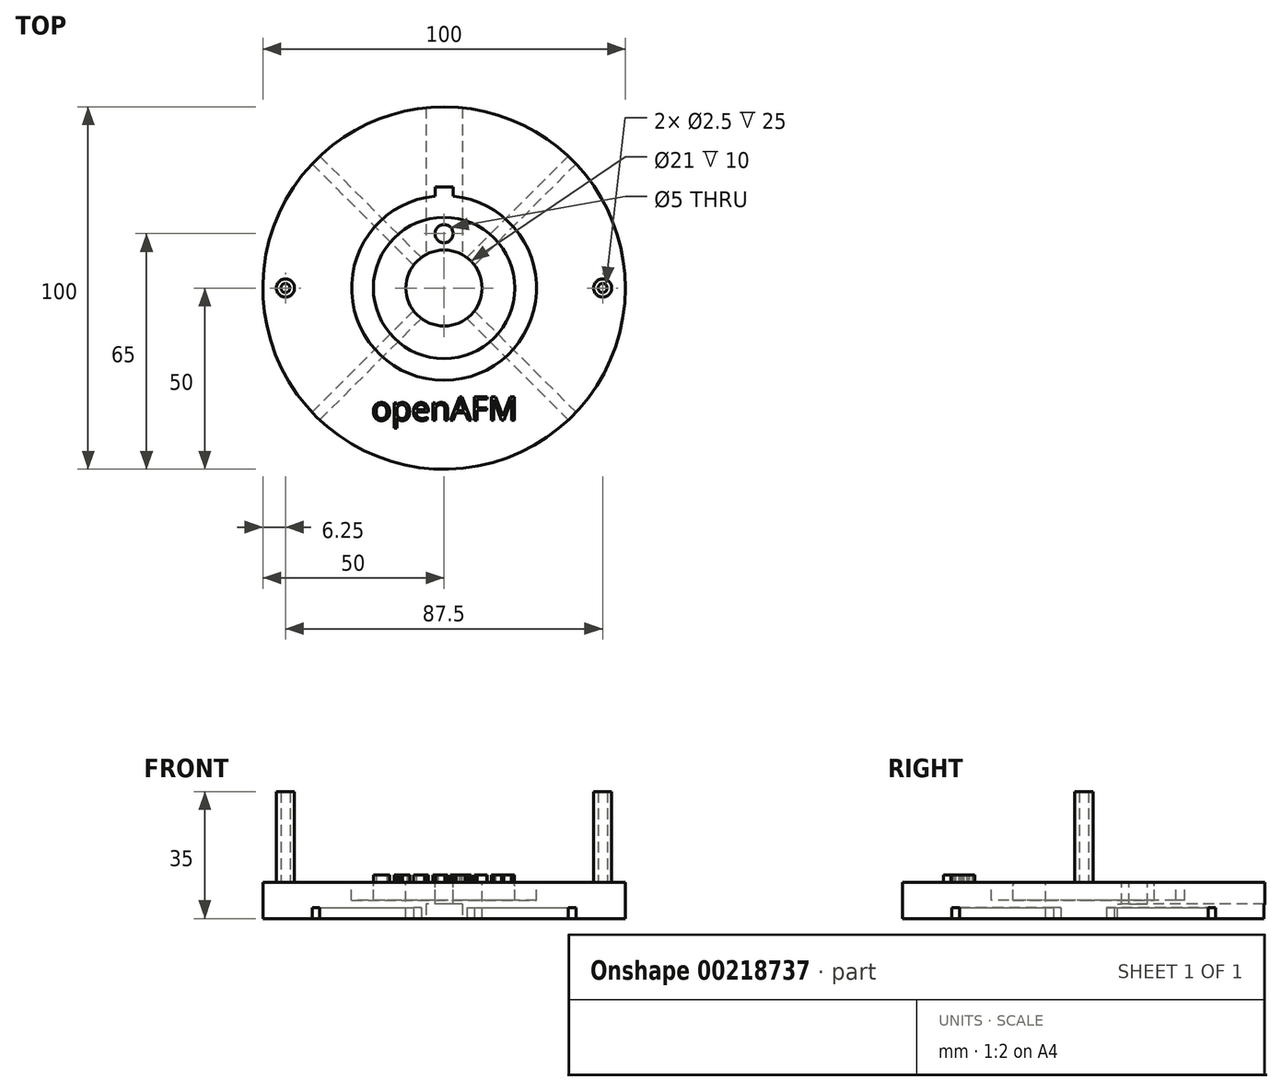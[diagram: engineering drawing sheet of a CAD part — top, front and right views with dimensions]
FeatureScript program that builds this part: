
annotation { "Feature Type Name" : "Feature", "Feature Type Description" : "" }
export const myFeature = defineFeature(function(context is Context, id is Id, definition is map)
    precondition{}
    {
        {
            var Q0;
            Q0=qCreatedBy(makeId("Top.planeOp"),FACE);
            var sketch = newSketch(context, id + "F0", { "sketchPlane" : qUnion([Q0])});
            skCircle(sketch, "E0", {"center": v(0, 0) * mm, "radius": 50 * mm});
            skSolve(sketch);
        }
        {
            var Q0;
            Q0=makeQuery(id+"F0.imprint","IMPRINT",FACE,{"disambiguationData":[TD([[makeQuery(id+"F0.imprint","IMPRINT",EDGE,{"derivedFrom":sQuery(id+"F0.wireOp",EDGE,"E0")}),1.0]])]});
            extrude(context, id + "F1", {"entities" : qUnion([Q0]), "depth" : 10 * mm});
        }
        {
            var Q0;
            Q0=makeQuery(id+"F1.opExtrude","CAP_FACE",FACE,{"disambiguationData":[OSD([sQuery(id+"F0.wireOp",EDGE,"E0")])],"isStart":false});
            var sketch = newSketch(context, id + "F2", { "sketchPlane" : qUnion([Q0])});
            skCircle(sketch, "E1", {"center": v(0, 0) * mm, "radius": 10.5 * mm});
            skSolve(sketch);
        }
        {
            var Q0;
            Q0=makeQuery(id+"F2.imprint","IMPRINT",FACE,{"disambiguationData":[TD([[makeQuery(id+"F2.imprint","IMPRINT",EDGE,{"derivedFrom":sQuery(id+"F2.wireOp",EDGE,"E1")}),1.0]])]});
            extrude(context, id + "F3", {"entities" : qUnion([Q0]), "operationType" : NewBodyOperationType.REMOVE, "oppositeDirection" : true, "depth" : 10 * mm});
        }
        {
            var Q0;
            Q0=makeQuery(id+"F1.opExtrude","CAP_FACE",FACE,{"disambiguationData":[OSD([sQuery(id+"F0.wireOp",EDGE,"E0")])],"isStart":true});
            var sketch = newSketch(context, id + "F4", { "sketchPlane" : qUnion([Q0])});
            skLineSegment(sketch, "E2", {"start": v(0, 0) * mm, "end": v(50, 0) * mm, "construction": true});
            skLineSegment(sketch, "E3", {"start": v(0, 0) * mm, "end": v(0, 50) * mm, "construction": true});
            skLineSegment(sketch, "E4", {"start": v(0, 0) * mm, "end": v(-50, 0) * mm, "construction": true});
            skLineSegment(sketch, "E5", {"start": v(0, 0) * mm, "end": v(0, -50) * mm, "construction": true});
            skLineSegment(sketch, "E6", {"start": v(0, 0) * mm, "end": v(-35.36, 35.36) * mm, "construction": true});
            skLineSegment(sketch, "E7", {"start": v(0, 0) * mm, "end": v(35.36, -35.36) * mm, "construction": true});
            skLineSegment(sketch, "E8", {"start": v(0, 0) * mm, "end": v(35.36, 35.36) * mm, "construction": true});
            skLineSegment(sketch, "E9", {"start": v(0, 0) * mm, "end": v(-35.36, -35.36) * mm, "construction": true});
            skLineSegment(sketch, "E10", {"start": v(-36.4, 34.28) * mm, "end": v(-8.4, 6.29) * mm});
            skLineSegment(sketch, "E11", {"start": v(-34.28, 36.4) * mm, "end": v(-6.29, 8.4) * mm});
            skArc(sketch, "E12", {"start": v(-8.4, -6.29) * mm, "mid": v(-7.42, -7.42) * mm, "end": v(-6.29, -8.4) * mm});
            skLineSegment(sketch, "E13.trimOffspring", {"start": v(6.29, -8.4) * mm, "end": v(34.28, -36.4) * mm});
            skLineSegment(sketch, "E14.trimOffspring", {"start": v(8.4, -6.29) * mm, "end": v(36.4, -34.28) * mm});
            skArc(sketch, "E15", {"start": v(-36.4, -34.28) * mm, "mid": v(-35.36, -35.36) * mm, "end": v(-34.28, -36.4) * mm});
            skLineSegment(sketch, "E16", {"start": v(-36.4, -34.28) * mm, "end": v(-8.4, -6.29) * mm});
            skLineSegment(sketch, "E17", {"start": v(-34.28, -36.4) * mm, "end": v(-6.29, -8.4) * mm});
            skLineSegment(sketch, "E18.trimOffspring", {"start": v(6.29, 8.4) * mm, "end": v(34.28, 36.4) * mm});
            skLineSegment(sketch, "E19.trimOffspring", {"start": v(8.4, 6.29) * mm, "end": v(36.4, 34.28) * mm});
            skArc(sketch, "E20.trimOffspring", {"start": v(-34.28, 36.4) * mm, "mid": v(-35.36, 35.36) * mm, "end": v(-36.4, 34.28) * mm});
            skArc(sketch, "E21.trimOffspring", {"start": v(36.4, 34.28) * mm, "mid": v(35.36, 35.36) * mm, "end": v(34.28, 36.4) * mm});
            skArc(sketch, "E22.trimOffspring", {"start": v(34.28, -36.4) * mm, "mid": v(35.36, -35.36) * mm, "end": v(36.4, -34.28) * mm});
            skArc(sketch, "E23.trimOffspring", {"start": v(-6.29, 8.4) * mm, "mid": v(-7.42, 7.42) * mm, "end": v(-8.4, 6.29) * mm});
            skArc(sketch, "E24.trimOffspring", {"start": v(8.4, 6.29) * mm, "mid": v(7.42, 7.42) * mm, "end": v(6.29, 8.4) * mm});
            skArc(sketch, "E25.trimOffspring", {"start": v(6.29, -8.4) * mm, "mid": v(7.42, -7.42) * mm, "end": v(8.4, -6.29) * mm});
            skLineSegment(sketch, "E26", {"start": v(-2.5, 10.2) * mm, "end": v(-2.5, 49.94) * mm});
            skLineSegment(sketch, "E27", {"start": v(2.5, 10.2) * mm, "end": v(2.5, 49.94) * mm});
            skLineSegment(sketch, "E28", {"start": v(2.5, 49.94) * mm, "end": v(2.93, 49.2) * mm});
            skArc(sketch, "E29", {"start": v(-2.5, 10.2) * mm, "mid": v(0, 10.5) * mm, "end": v(2.5, 10.2) * mm});
            skArc(sketch, "E30", {"start": v(-2.5, 49.94) * mm, "mid": v(0, 50) * mm, "end": v(2.5, 49.94) * mm});
            skSolve(sketch);
        }
        {
            var Q0;
            Q0=makeQuery(id+"F4.imprint","IMPRINT",FACE,{"disambiguationData":[TD([[makeQuery(id+"F4.imprint","IMPRINT",EDGE,{"derivedFrom":sQuery(id+"F4.wireOp",EDGE,"E10")}),1.0]])]});
            var Q1;
            Q1=makeQuery(id+"F4.imprint","IMPRINT",FACE,{"disambiguationData":[TD([[makeQuery(id+"F4.imprint","IMPRINT",EDGE,{"derivedFrom":sQuery(id+"F4.wireOp",EDGE,"E18.trimOffspring")}),-1.0]])]});
            var Q2;
            Q2=makeQuery(id+"F4.imprint","IMPRINT",FACE,{"disambiguationData":[TD([[makeQuery(id+"F4.imprint","IMPRINT",EDGE,{"derivedFrom":sQuery(id+"F4.wireOp",EDGE,"E13.trimOffspring")}),1.0]])]});
            var Q3;
            Q3=makeQuery(id+"F4.imprint","IMPRINT",FACE,{"disambiguationData":[TD([[makeQuery(id+"F4.imprint","IMPRINT",EDGE,{"derivedFrom":sQuery(id+"F4.wireOp",EDGE,"E12")}),1.0]])]});
            extrude(context, id + "F5", {"entities" : qUnion([Q0, Q1, Q2, Q3]), "operationType" : NewBodyOperationType.REMOVE, "oppositeDirection" : true, "depth" : 3 * mm});
        }
        {
            var Q0;
            Q0=makeQuery(id+"F1.opExtrude","CAP_FACE",FACE,{"disambiguationData":[OSD([sQuery(id+"F0.wireOp",EDGE,"E0")])],"isStart":false});
            var sketch = newSketch(context, id + "F6", { "sketchPlane" : qUnion([Q0])});
            skCircle(sketch, "E31", {"center": v(0, 0) * mm, "radius": 19.5 * mm});
            skCircle(sketch, "E32", {"center": v(0, 0) * mm, "radius": 25.5 * mm});
            skSolve(sketch);
        }
        {
            var Q0;
            Q0=makeQuery(id+"F6.imprint","IMPRINT",FACE,{"disambiguationData":[TD([[makeQuery(id+"F6.imprint","IMPRINT",EDGE,{"derivedFrom":sQuery(id+"F6.wireOp",EDGE,"E31")}),-1.0]])]});
            extrude(context, id + "F7", {"entities" : qUnion([Q0]), "operationType" : NewBodyOperationType.REMOVE, "oppositeDirection" : true, "depth" : 5 * mm});
        }
        {
            var Q0;
            {var subQ0=sQuery(id+"F0.wireOp",EDGE,"E0");Q0=makeQuery(id+"F7.boolean.opBoolean","SPLIT",FACE,{"disambiguationData":[TD([makeQuery(id+"F1.opExtrude","SWEPT_FACE",FACE,{"disambiguationData":[OSD([subQ0])]})])],"derivedFrom":makeQuery(id+"F1.opExtrude","CAP_FACE",FACE,{"disambiguationData":[OSD([subQ0])],"isStart":false})});}
            var sketch = newSketch(context, id + "F8", { "sketchPlane" : qUnion([Q0])});
            skCircle(sketch, "E33", {"center": v(-43.75, 0) * mm, "radius": 2.5 * mm});
            skCircle(sketch, "E34", {"center": v(-43.75, 0) * mm, "radius": 1.25 * mm});
            skCircle(sketch, "E35", {"center": v(43.75, 0) * mm, "radius": 2.5 * mm});
            skCircle(sketch, "E36", {"center": v(43.75, 0) * mm, "radius": 1.25 * mm});
            skSolve(sketch);
        }
        {
            var Q0;
            Q0 = qSketchRegion(id + "F8", true);
            extrude(context, id + "F9", {"entities" : qUnion([Q0]), "operationType" : NewBodyOperationType.ADD, "depth" : 25 * mm});
        }
        {
            var Q0;
            Q0=makeQuery(id+"F7.boolean.opBoolean","COPY",EDGE,{"derivedFrom":makeQuery(id+"F7.opExtrude","CAP_EDGE",EDGE,{"disambiguationData":[OSD([sQuery(id+"F6.wireOp",EDGE,"E31")])],"isStart":true})});
            var Q1;
            Q1=makeQuery(id+"F7.boolean.opBoolean","COPY",EDGE,{"derivedFrom":makeQuery(id+"F7.opExtrude","CAP_EDGE",EDGE,{"disambiguationData":[OSD([sQuery(id+"F6.wireOp",EDGE,"E32")])],"isStart":true})});
            fillet(context, id + "F10", {"entities" : qUnion([Q0, Q1]), "radius" : 1 * mm, "tangentPropagation" : true, "allowEdgeOverflow" : false});
        }
        {
            var Q0;
            Q0=makeQuery(id+"F7.boolean.opBoolean","SPLIT",FACE,{"disambiguationData":[TD([makeQuery(id+"F3.boolean.opBoolean","COPY",FACE,{"derivedFrom":makeQuery(id+"F3.opExtrude","SWEPT_FACE",FACE,{"disambiguationData":[OSD([sQuery(id+"F2.wireOp",EDGE,"E1")])]})})])],"derivedFrom":makeQuery(id+"F1.opExtrude","CAP_FACE",FACE,{"disambiguationData":[OSD([sQuery(id+"F0.wireOp",EDGE,"E0")])],"isStart":false})});
            var sketch = newSketch(context, id + "F11", { "sketchPlane" : qUnion([Q0])});
            skCircle(sketch, "E37", {"center": v(0, 15) * mm, "radius": 2.5 * mm});
            skSolve(sketch);
        }
        {
            var Q0;
            Q0 = qSketchRegion(id + "F11", true);
            extrude(context, id + "F12", {"entities" : qUnion([Q0]), "operationType" : NewBodyOperationType.REMOVE, "oppositeDirection" : true, "depth" : 10 * mm});
        }
        {
            var Q0;
            Q0=qCreatedBy(makeId("Front.planeOp"),FACE);
            var sketch = newSketch(context, id + "F13", { "sketchPlane" : qUnion([Q0])});
            skLineSegment(sketch, "E38", {"start": v(-5, 4) * mm, "end": v(-5, 0) * mm});
            skLineSegment(sketch, "E39", {"start": v(-5, 0) * mm, "end": v(5, 0) * mm});
            skLineSegment(sketch, "E40", {"start": v(5, 0) * mm, "end": v(5, 4) * mm});
            skLineSegment(sketch, "E41", {"start": v(5, 4) * mm, "end": v(-5, 4) * mm});
            skSolve(sketch);
        }
        {
            var Q0;
            Q0 = qSketchRegion(id + "F13", true);
            extrude(context, id + "F14", {"entities" : qUnion([Q0]), "operationType" : NewBodyOperationType.REMOVE, "oppositeDirection" : true, "depth" : 50 * mm});
        }
        {
            var Q0;
            {var subQ0=sQuery(id+"F0.wireOp",EDGE,"E0");var subQ1=makeQuery(id+"F1.opExtrude","SWEPT_FACE",FACE,{"disambiguationData":[OSD([subQ0])]});Q0=makeQuery(id+"F9.boolean.opBoolean","SPLIT",FACE,{"disambiguationData":[TD([subQ1])],"derivedFrom":makeQuery(id+"F7.boolean.opBoolean","SPLIT",FACE,{"disambiguationData":[TD([subQ1])],"derivedFrom":makeQuery(id+"F1.opExtrude","CAP_FACE",FACE,{"disambiguationData":[OSD([subQ0])],"isStart":false})})});}
            var sketch = newSketch(context, id + "F15", { "sketchPlane" : qUnion([Q0])});
            skArc(sketch, "E42", {"start": v(2.5, 25.38) * mm, "mid": v(0, 25.5) * mm, "end": v(-2.5, 25.38) * mm});
            skLineSegment(sketch, "E43", {"start": v(0, 0) * mm, "end": v(0, 32.13) * mm, "construction": true});
            skLineSegment(sketch, "E44", {"start": v(-2.5, 25.38) * mm, "end": v(-2.5, 27.88) * mm});
            skLineSegment(sketch, "E45", {"start": v(-2.5, 27.88) * mm, "end": v(2.5, 27.88) * mm});
            skLineSegment(sketch, "E46", {"start": v(2.5, 27.88) * mm, "end": v(2.5, 25.38) * mm});
            skSolve(sketch);
        }
        {
            var Q0;
            Q0 = qSketchRegion(id + "F15", true);
            extrude(context, id + "F16", {"entities" : qUnion([Q0]), "operationType" : NewBodyOperationType.REMOVE, "oppositeDirection" : true, "depth" : 5 * mm});
        }
        {
            var Q0;
            {var subQ0=sQuery(id+"F0.wireOp",EDGE,"E0");var subQ1=makeQuery(id+"F1.opExtrude","SWEPT_FACE",FACE,{"disambiguationData":[OSD([subQ0])]});Q0=makeQuery(id+"F9.boolean.opBoolean","SPLIT",FACE,{"disambiguationData":[TD([subQ1])],"derivedFrom":makeQuery(id+"F7.boolean.opBoolean","SPLIT",FACE,{"disambiguationData":[TD([subQ1])],"derivedFrom":makeQuery(id+"F1.opExtrude","CAP_FACE",FACE,{"disambiguationData":[OSD([subQ0])],"isStart":false})})});}
            var sketch = newSketch(context, id + "F17", { "sketchPlane" : qUnion([Q0])});
            skText(sketch, "E47", { "text": "openAFM\n", "fontName": "OpenSans-Regular.ttf"});
            const initialGuessF17  = {"E47": [-0.02, -0.03653, 1, 0, 0.00653]};
            skSetInitialGuess(sketch, initialGuessF17);
            skSolve(sketch);
        }
        {
            var Q0;
            Q0 = qSketchRegion(id + "F17", true);
            extrude(context, id + "F18", {"entities" : qUnion([Q0]), "operationType" : NewBodyOperationType.ADD, "depth" : 2 * mm});
        }
    });
